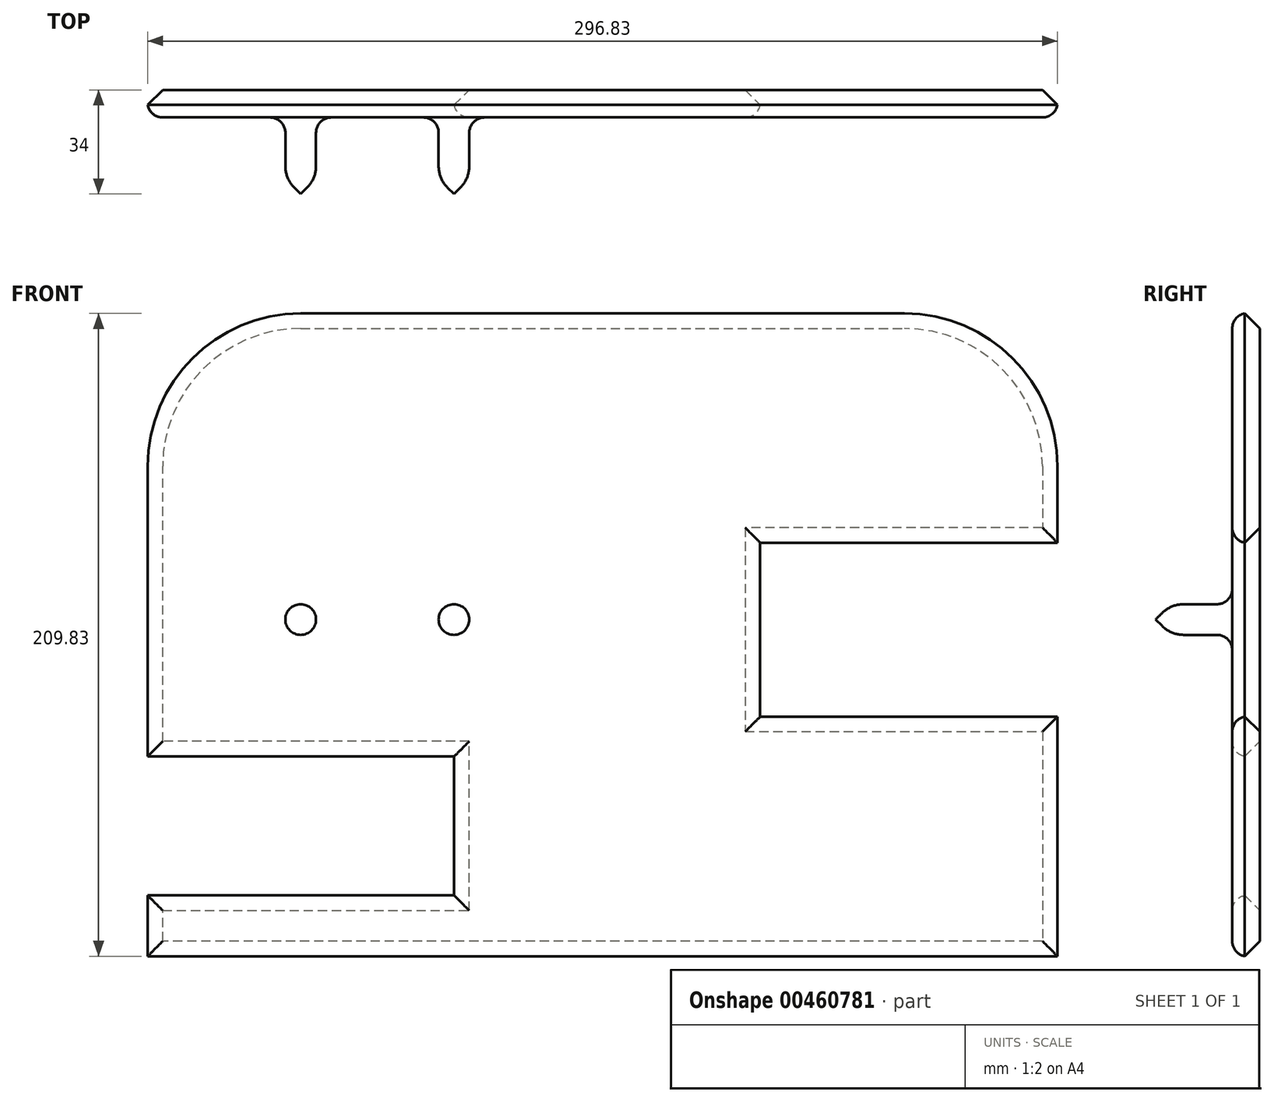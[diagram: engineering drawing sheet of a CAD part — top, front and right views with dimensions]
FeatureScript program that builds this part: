
annotation { "Feature Type Name" : "Feature", "Feature Type Description" : "" }
export const myFeature = defineFeature(function(context is Context, id is Id, definition is map)
    precondition{}
    {
        {
            var Q0;
            Q0=qCreatedBy(makeId("Front.planeOp"),FACE);
            var sketch = newSketch(context, id + "F0", { "sketchPlane" : qUnion([Q0])});
            skLineSegment(sketch, "E0.bottom", {"start": v(-96.93, 56.54) * mm, "end": v(100.07, 56.54) * mm});
            skLineSegment(sketch, "E0.top", {"start": v(-146.93, -153.46) * mm, "end": v(150.07, -153.46) * mm});
            skLineSegment(sketch, "E0.left", {"start": v(-146.93, 6.54) * mm, "end": v(-146.93, -153.46) * mm});
            skLineSegment(sketch, "E0.right", {"start": v(150.07, 6.54) * mm, "end": v(150.07, -153.46) * mm});
            skPoint(sketch, "E1.visualSharp", {"position": v(-146.93, 56.54) * mm});
            skArc(sketch, "E1.filletArc", {"start": v(-96.93, 56.54) * mm, "mid": v(-132.29, 41.9) * mm, "end": v(-146.93, 6.54) * mm});
            skPoint(sketch, "E2.visualSharp", {"position": v(150.07, 56.54) * mm});
            skArc(sketch, "E2.filletArc", {"start": v(150.07, 6.54) * mm, "mid": v(135.42, 41.9) * mm, "end": v(100.07, 56.54) * mm});
            skSolve(sketch);
        }
        {
            var Q0;
            Q0=makeQuery(id+"F0.imprint","IMPRINT",FACE,{"disambiguationData":[TD([[makeQuery(id+"F0.imprint","IMPRINT",EDGE,{"derivedFrom":sQuery(id+"F0.wireOp",EDGE,"E0.bottom")}),-1.0]])]});
            extrude(context, id + "F1", {"entities" : qUnion([Q0]), "depth" : 9 * mm});
        }
        {
            var Q0;
            Q0=makeQuery(id+"F1.opExtrude","CAP_FACE",FACE,{"disambiguationData":[OSD([sQuery(id+"F0.wireOp",EDGE,"E0.bottom"),sQuery(id+"F0.wireOp",EDGE,"E0.top"),sQuery(id+"F0.wireOp",EDGE,"E0.left"),sQuery(id+"F0.wireOp",EDGE,"E0.right"),sQuery(id+"F0.wireOp",EDGE,"E1.filletArc"),sQuery(id+"F0.wireOp",EDGE,"E2.filletArc")])],"isStart":false});
            var sketch = newSketch(context, id + "F2", { "sketchPlane" : qUnion([Q0])});
            skCircle(sketch, "E3", {"center": v(-46.93, -43.46) * mm, "radius": 5 * mm});
            skCircle(sketch, "E4", {"center": v(-96.93, -43.46) * mm, "radius": 5 * mm});
            skSolve(sketch);
        }
        {
            var Q0;
            Q0=makeQuery(id+"F2.imprint","IMPRINT",FACE,{"disambiguationData":[TD([[makeQuery(id+"F2.imprint","IMPRINT",EDGE,{"derivedFrom":sQuery(id+"F2.wireOp",EDGE,"E3")}),1.0]])]});
            var Q1;
            Q1=makeQuery(id+"F2.imprint","IMPRINT",FACE,{"disambiguationData":[TD([[makeQuery(id+"F2.imprint","IMPRINT",EDGE,{"derivedFrom":sQuery(id+"F2.wireOp",EDGE,"E4")}),1.0]])]});
            extrude(context, id + "F3", {"entities" : qUnion([Q0, Q1]), "operationType" : NewBodyOperationType.ADD, "depth" : 25 * mm});
        }
        {
            var Q0;
            Q0=makeQuery(id+"F2.imprint","IMPRINT",FACE,{"disambiguationData":[TD([[makeQuery(id+"F2.imprint","IMPRINT",EDGE,{"derivedFrom":sQuery(id+"F2.wireOp",EDGE,"E3")}),-1.0]])]});
            var sketch = newSketch(context, id + "F4", { "sketchPlane" : qUnion([Q0])});
            skLineSegment(sketch, "E5.bottom", {"start": v(53.07, -18.46) * mm, "end": v(157.07, -18.46) * mm});
            skLineSegment(sketch, "E5.top", {"start": v(53.07, -75.07) * mm, "end": v(157.07, -75.07) * mm});
            skLineSegment(sketch, "E5.left", {"start": v(53.07, -18.46) * mm, "end": v(53.07, -75.07) * mm});
            skLineSegment(sketch, "E5.right", {"start": v(157.07, -18.46) * mm, "end": v(157.07, -75.07) * mm});
            skSolve(sketch);
        }
        {
            var Q0;
            Q0 = qSketchRegion(id + "F4", true);
            extrude(context, id + "F5", {"entities" : qUnion([Q0]), "operationType" : NewBodyOperationType.REMOVE, "oppositeDirection" : true, "depth" : 25 * mm});
        }
        {
            var Q0;
            {var subQ2=sQuery(id+"F4.wireOp",EDGE,"E5.left");Q0=makeQuery(id+"F4.imprint","IMPRINT",FACE,{"disambiguationData":[TD([[makeQuery(id+"F4.imprint","IMPRINT",EDGE,{"derivedFrom":subQ2}),-1.0]])]});}
            var sketch = newSketch(context, id + "F6", { "sketchPlane" : qUnion([Q0])});
            skLineSegment(sketch, "E6.bottom", {"start": v(-160.09, -88.22) * mm, "end": v(-46.93, -88.22) * mm});
            skLineSegment(sketch, "E6.top", {"start": v(-160.09, -133.46) * mm, "end": v(-46.93, -133.46) * mm});
            skLineSegment(sketch, "E6.left", {"start": v(-160.09, -88.22) * mm, "end": v(-160.09, -133.46) * mm});
            skLineSegment(sketch, "E6.right", {"start": v(-46.93, -88.22) * mm, "end": v(-46.93, -133.46) * mm});
            skSolve(sketch);
        }
        {
            var Q0;
            Q0 = qSketchRegion(id + "F6", true);
            extrude(context, id + "F7", {"entities" : qUnion([Q0]), "operationType" : NewBodyOperationType.REMOVE, "oppositeDirection" : true, "depth" : 25 * mm});
        }
        {
            var Q0;
            Q0=makeQuery(id+"F1.opExtrude","CAP_FACE",FACE,{"disambiguationData":[OSD([sQuery(id+"F0.wireOp",EDGE,"E0.bottom"),sQuery(id+"F0.wireOp",EDGE,"E0.top"),sQuery(id+"F0.wireOp",EDGE,"E0.left"),sQuery(id+"F0.wireOp",EDGE,"E0.right"),sQuery(id+"F0.wireOp",EDGE,"E1.filletArc"),sQuery(id+"F0.wireOp",EDGE,"E2.filletArc")])],"isStart":false});
            fillet(context, id + "F8", {"entities" : qUnion([Q0]), "radius" : 5 * mm, "tangentPropagation" : true, "allowEdgeOverflow" : false});
        }
        {
            var Q0;
            Q0=makeQuery(id+"F3.opExtrude","CAP_EDGE",EDGE,{"disambiguationData":[OSD([sQuery(id+"F2.wireOp",EDGE,"E4")])],"isStart":false});
            var Q1;
            Q1=makeQuery(id+"F3.opExtrude","CAP_EDGE",EDGE,{"disambiguationData":[OSD([sQuery(id+"F2.wireOp",EDGE,"E3")])],"isStart":false});
            chamfer(context, id + "F9", {"entities" : qUnion([Q0, Q1]), "width" : 5 * mm, "tangentPropagation" : true});
        }
        {
            var Q0;
            Q0=makeQuery(id+"F9.opChamfer","BLEND_FACE",FACE,{"disambiguationData":[OSD([sQuery(id+"F2.wireOp",EDGE,"E4")])]});
            var Q1;
            Q1=makeQuery(id+"F9.opChamfer","BLEND_FACE",FACE,{"disambiguationData":[OSD([sQuery(id+"F2.wireOp",EDGE,"E3")])]});
            fillet(context, id + "F10", {"entities" : qUnion([Q0, Q1]), "radius" : 10 * mm, "tangentPropagation" : true, "allowEdgeOverflow" : false});
        }
        {
            var Q0;
            Q0=makeQuery(id+"F1.opExtrude","CAP_FACE",FACE,{"disambiguationData":[OSD([sQuery(id+"F0.wireOp",EDGE,"E0.bottom"),sQuery(id+"F0.wireOp",EDGE,"E0.top"),sQuery(id+"F0.wireOp",EDGE,"E0.left"),sQuery(id+"F0.wireOp",EDGE,"E0.right"),sQuery(id+"F0.wireOp",EDGE,"E1.filletArc"),sQuery(id+"F0.wireOp",EDGE,"E2.filletArc")])],"isStart":true});
            chamfer(context, id + "F11", {"entities" : qUnion([Q0]), "width" : 5 * mm, "tangentPropagation" : true});
        }
    });
